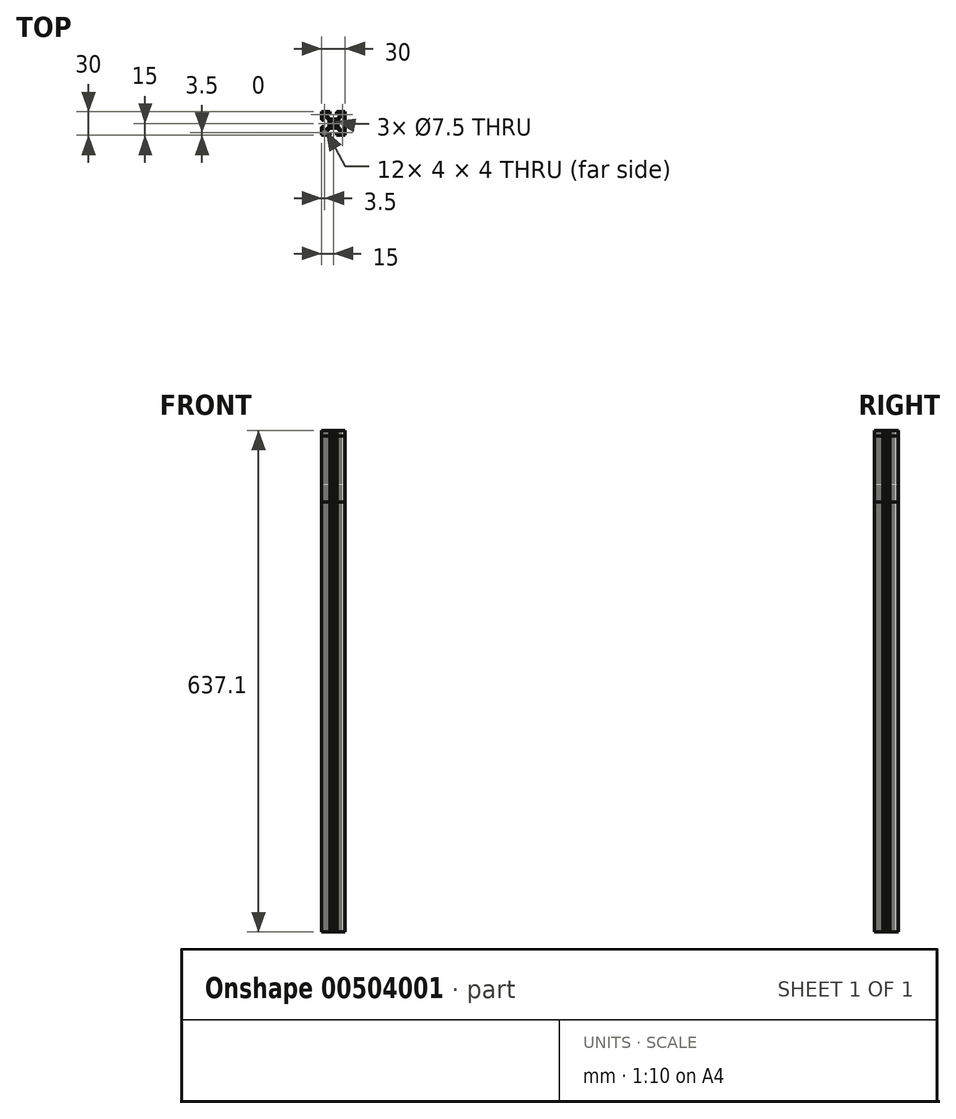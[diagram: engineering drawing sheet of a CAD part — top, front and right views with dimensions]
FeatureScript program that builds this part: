
annotation { "Feature Type Name" : "Feature", "Feature Type Description" : "" }
export const myFeature = defineFeature(function(context is Context, id is Id, definition is map)
    precondition{}
    {
        {
            assignVariable(context, id + "F0", {"name" : "Y", "anyValue" : 630});
        }
        {
            var Q0;
            Q0=qCreatedBy(makeId("Top.planeOp"),FACE);
            var sketch = newSketch(context, id + "F1", { "sketchPlane" : qUnion([Q0])});
            skLineSegment(sketch, "E0", {"start": v(-14.5, 4.6) * mm, "end": v(-15, 4.6) * mm});
            skLineSegment(sketch, "E1", {"start": v(-14.5, 4.1) * mm, "end": v(-14.5, 4.6) * mm});
            skLineSegment(sketch, "E2", {"start": v(-12.8, 4.1) * mm, "end": v(-14.5, 4.1) * mm});
            skLineSegment(sketch, "E3", {"start": v(-12.8, 8.4) * mm, "end": v(-12.8, 4.1) * mm});
            skLineSegment(sketch, "E4", {"start": v(-9.81, 8.4) * mm, "end": v(-12.8, 8.4) * mm});
            skLineSegment(sketch, "E5", {"start": v(-5.75, 0.5) * mm, "end": v(-5.75, 4.34) * mm});
            skLineSegment(sketch, "E6", {"start": v(-5.25, 0) * mm, "end": v(-5.75, 0.5) * mm});
            skLineSegment(sketch, "E7", {"start": v(-5.75, -0.5) * mm, "end": v(-5.25, 0) * mm});
            skLineSegment(sketch, "E8", {"start": v(-5.75, -4.34) * mm, "end": v(-5.75, -0.5) * mm});
            skLineSegment(sketch, "E9", {"start": v(-12.8, -8.4) * mm, "end": v(-9.81, -8.4) * mm});
            skLineSegment(sketch, "E10", {"start": v(-12.8, -4.1) * mm, "end": v(-12.8, -8.4) * mm});
            skLineSegment(sketch, "E11", {"start": v(-14.5, -4.1) * mm, "end": v(-12.8, -4.1) * mm});
            skLineSegment(sketch, "E12", {"start": v(-14.5, -4.6) * mm, "end": v(-14.5, -4.1) * mm});
            skLineSegment(sketch, "E13", {"start": v(-15, -4.6) * mm, "end": v(-14.5, -4.6) * mm});
            skLineSegment(sketch, "E14", {"start": v(-4.6, -14.5) * mm, "end": v(-4.6, -15) * mm});
            skLineSegment(sketch, "E15", {"start": v(-4.1, -14.5) * mm, "end": v(-4.6, -14.5) * mm});
            skLineSegment(sketch, "E16", {"start": v(-4.1, -12.8) * mm, "end": v(-4.1, -14.5) * mm});
            skLineSegment(sketch, "E17", {"start": v(-8.4, -12.8) * mm, "end": v(-4.1, -12.8) * mm});
            skLineSegment(sketch, "E18", {"start": v(-8.4, -9.81) * mm, "end": v(-8.4, -12.8) * mm});
            skLineSegment(sketch, "E19", {"start": v(-0.5, -5.75) * mm, "end": v(-4.34, -5.75) * mm});
            skLineSegment(sketch, "E20", {"start": v(0, -5.25) * mm, "end": v(-0.5, -5.75) * mm});
            skLineSegment(sketch, "E21", {"start": v(0.5, -5.75) * mm, "end": v(0, -5.25) * mm});
            skLineSegment(sketch, "E22", {"start": v(4.34, -5.75) * mm, "end": v(0.5, -5.75) * mm});
            skLineSegment(sketch, "E23", {"start": v(8.4, -12.8) * mm, "end": v(8.4, -9.81) * mm});
            skLineSegment(sketch, "E24", {"start": v(4.1, -12.8) * mm, "end": v(8.4, -12.8) * mm});
            skLineSegment(sketch, "E25", {"start": v(4.1, -14.5) * mm, "end": v(4.1, -12.8) * mm});
            skLineSegment(sketch, "E26", {"start": v(4.6, -14.5) * mm, "end": v(4.1, -14.5) * mm});
            skLineSegment(sketch, "E27", {"start": v(4.6, -15) * mm, "end": v(4.6, -14.5) * mm});
            skLineSegment(sketch, "E28", {"start": v(14.5, -4.6) * mm, "end": v(15, -4.6) * mm});
            skLineSegment(sketch, "E29", {"start": v(14.5, -4.1) * mm, "end": v(14.5, -4.6) * mm});
            skLineSegment(sketch, "E30", {"start": v(12.8, -4.1) * mm, "end": v(14.5, -4.1) * mm});
            skLineSegment(sketch, "E31", {"start": v(12.8, -8.4) * mm, "end": v(12.8, -4.1) * mm});
            skLineSegment(sketch, "E32", {"start": v(9.81, -8.4) * mm, "end": v(12.8, -8.4) * mm});
            skLineSegment(sketch, "E33", {"start": v(5.75, -0.5) * mm, "end": v(5.75, -4.34) * mm});
            skLineSegment(sketch, "E34", {"start": v(5.25, 0) * mm, "end": v(5.75, -0.5) * mm});
            skLineSegment(sketch, "E35", {"start": v(5.75, 0.5) * mm, "end": v(5.25, 0) * mm});
            skLineSegment(sketch, "E36", {"start": v(5.75, 4.34) * mm, "end": v(5.75, 0.5) * mm});
            skLineSegment(sketch, "E37", {"start": v(12.8, 8.4) * mm, "end": v(9.81, 8.4) * mm});
            skLineSegment(sketch, "E38", {"start": v(12.8, 4.1) * mm, "end": v(12.8, 8.4) * mm});
            skLineSegment(sketch, "E39", {"start": v(14.5, 4.1) * mm, "end": v(12.8, 4.1) * mm});
            skLineSegment(sketch, "E40", {"start": v(14.5, 4.6) * mm, "end": v(14.5, 4.1) * mm});
            skLineSegment(sketch, "E41", {"start": v(15, 4.6) * mm, "end": v(14.5, 4.6) * mm});
            skLineSegment(sketch, "E42", {"start": v(4.6, 14.5) * mm, "end": v(4.6, 15) * mm});
            skLineSegment(sketch, "E43", {"start": v(4.1, 14.5) * mm, "end": v(4.6, 14.5) * mm});
            skLineSegment(sketch, "E44", {"start": v(4.1, 12.8) * mm, "end": v(4.1, 14.5) * mm});
            skLineSegment(sketch, "E45", {"start": v(8.4, 12.8) * mm, "end": v(4.1, 12.8) * mm});
            skLineSegment(sketch, "E46", {"start": v(8.4, 9.81) * mm, "end": v(8.4, 12.8) * mm});
            skLineSegment(sketch, "E47", {"start": v(0.5, 5.75) * mm, "end": v(4.34, 5.75) * mm});
            skLineSegment(sketch, "E48", {"start": v(0, 5.25) * mm, "end": v(0.5, 5.75) * mm});
            skLineSegment(sketch, "E49", {"start": v(-0.5, 5.75) * mm, "end": v(0, 5.25) * mm});
            skLineSegment(sketch, "E50", {"start": v(-4.34, 5.75) * mm, "end": v(-0.5, 5.75) * mm});
            skLineSegment(sketch, "E51", {"start": v(-8.4, 12.8) * mm, "end": v(-8.4, 9.81) * mm});
            skLineSegment(sketch, "E52", {"start": v(-4.1, 12.8) * mm, "end": v(-8.4, 12.8) * mm});
            skLineSegment(sketch, "E53", {"start": v(-4.1, 14.5) * mm, "end": v(-4.1, 12.8) * mm});
            skLineSegment(sketch, "E54", {"start": v(-4.6, 14.5) * mm, "end": v(-4.1, 14.5) * mm});
            skLineSegment(sketch, "E55", {"start": v(-4.6, 15) * mm, "end": v(-4.6, 14.5) * mm});
            skLineSegment(sketch, "E56", {"start": v(13.5, 13.5) * mm, "end": v(9.5, 13.5) * mm});
            skLineSegment(sketch, "E57", {"start": v(13.5, 9.5) * mm, "end": v(13.5, 13.5) * mm});
            skLineSegment(sketch, "E58", {"start": v(9.5, 9.5) * mm, "end": v(13.5, 9.5) * mm});
            skLineSegment(sketch, "E59", {"start": v(9.5, 13.5) * mm, "end": v(9.5, 9.5) * mm});
            skLineSegment(sketch, "E60", {"start": v(-9.5, 9.5) * mm, "end": v(-9.5, 13.5) * mm});
            skLineSegment(sketch, "E61", {"start": v(-13.5, 9.5) * mm, "end": v(-9.5, 9.5) * mm});
            skLineSegment(sketch, "E62", {"start": v(-13.5, 13.5) * mm, "end": v(-13.5, 9.5) * mm});
            skLineSegment(sketch, "E63", {"start": v(-9.5, 13.5) * mm, "end": v(-13.5, 13.5) * mm});
            skLineSegment(sketch, "E64", {"start": v(-9.5, -13.5) * mm, "end": v(-9.5, -9.5) * mm});
            skLineSegment(sketch, "E65", {"start": v(-13.5, -13.5) * mm, "end": v(-9.5, -13.5) * mm});
            skLineSegment(sketch, "E66", {"start": v(-13.5, -9.5) * mm, "end": v(-13.5, -13.5) * mm});
            skLineSegment(sketch, "E67", {"start": v(-9.5, -9.5) * mm, "end": v(-13.5, -9.5) * mm});
            skLineSegment(sketch, "E68", {"start": v(13.5, -9.5) * mm, "end": v(9.5, -9.5) * mm});
            skLineSegment(sketch, "E69", {"start": v(13.5, -13.5) * mm, "end": v(13.5, -9.5) * mm});
            skLineSegment(sketch, "E70", {"start": v(9.5, -13.5) * mm, "end": v(13.5, -13.5) * mm});
            skLineSegment(sketch, "E71", {"start": v(9.5, -9.5) * mm, "end": v(9.5, -13.5) * mm});
            skCircle(sketch, "E72", {"center": v(0, 0) * mm, "radius": 3.75 * mm});
            skLineSegment(sketch, "E73", {"start": v(-15, -4.6) * mm, "end": v(-15, -15) * mm});
            skLineSegment(sketch, "E74", {"start": v(15, -4.6) * mm, "end": v(15, -15) * mm});
            skLineSegment(sketch, "E75", {"start": v(-4.6, -15) * mm, "end": v(-15, -15) * mm});
            skLineSegment(sketch, "E76", {"start": v(-9.81, -8.4) * mm, "end": v(-5.75, -4.34) * mm});
            skLineSegment(sketch, "E77", {"start": v(-8.4, -9.81) * mm, "end": v(-4.34, -5.75) * mm});
            skLineSegment(sketch, "E78", {"start": v(4.6, -15) * mm, "end": v(15, -15) * mm});
            skLineSegment(sketch, "E79", {"start": v(4.34, -5.75) * mm, "end": v(8.4, -9.81) * mm});
            skLineSegment(sketch, "E80", {"start": v(5.75, -4.34) * mm, "end": v(9.81, -8.4) * mm});
            skLineSegment(sketch, "E81", {"start": v(9.81, 8.4) * mm, "end": v(5.75, 4.34) * mm});
            skLineSegment(sketch, "E82", {"start": v(8.4, 9.81) * mm, "end": v(4.34, 5.75) * mm});
            skLineSegment(sketch, "E83", {"start": v(-9.81, 8.4) * mm, "end": v(-5.75, 4.34) * mm});
            skLineSegment(sketch, "E84", {"start": v(-8.4, 9.81) * mm, "end": v(-4.34, 5.75) * mm});
            skLineSegment(sketch, "E85", {"start": v(-15, 4.6) * mm, "end": v(-15, 15) * mm});
            skLineSegment(sketch, "E86", {"start": v(15, 4.6) * mm, "end": v(15, 15) * mm});
            skLineSegment(sketch, "E87", {"start": v(-4.6, 15) * mm, "end": v(-15, 15) * mm});
            skLineSegment(sketch, "E88", {"start": v(15, 15) * mm, "end": v(4.6, 15) * mm});
            skSolve(sketch);
        }
        {
            var Q0;
            Q0=makeQuery(id+"F1.imprint","IMPRINT",FACE,{"disambiguationData":[TD([[makeQuery(id+"F1.imprint","IMPRINT",EDGE,{"derivedFrom":sQuery(id+"F1.wireOp",EDGE,"E0")}),-1.0]])]});
            extrude(context, id + "F2", {"entities" : qUnion([Q0]), "depth" : 546 * mm, "offsetDistance" : 25 * mm});
        }
        {
            var Q0;
            Q0=qCreatedBy(makeId("Top.planeOp"),FACE);
            var sketch = newSketch(context, id + "F3", { "sketchPlane" : qUnion([Q0])});
            skLineSegment(sketch, "E89", {"start": v(-14.5, 4.6) * mm, "end": v(-15, 4.6) * mm});
            skLineSegment(sketch, "E90", {"start": v(-14.5, 4.1) * mm, "end": v(-14.5, 4.6) * mm});
            skLineSegment(sketch, "E91", {"start": v(-12.8, 4.1) * mm, "end": v(-14.5, 4.1) * mm});
            skLineSegment(sketch, "E92", {"start": v(-12.8, 8.4) * mm, "end": v(-12.8, 4.1) * mm});
            skLineSegment(sketch, "E93", {"start": v(-9.81, 8.4) * mm, "end": v(-12.8, 8.4) * mm});
            skLineSegment(sketch, "E94", {"start": v(-5.75, 0.5) * mm, "end": v(-5.75, 4.34) * mm});
            skLineSegment(sketch, "E95", {"start": v(-5.25, 0) * mm, "end": v(-5.75, 0.5) * mm});
            skLineSegment(sketch, "E96", {"start": v(-5.75, -0.5) * mm, "end": v(-5.25, 0) * mm});
            skLineSegment(sketch, "E97", {"start": v(-5.75, -4.34) * mm, "end": v(-5.75, -0.5) * mm});
            skLineSegment(sketch, "E98", {"start": v(-12.8, -8.4) * mm, "end": v(-9.81, -8.4) * mm});
            skLineSegment(sketch, "E99", {"start": v(-12.8, -4.1) * mm, "end": v(-12.8, -8.4) * mm});
            skLineSegment(sketch, "E100", {"start": v(-14.5, -4.1) * mm, "end": v(-12.8, -4.1) * mm});
            skLineSegment(sketch, "E101", {"start": v(-14.5, -4.6) * mm, "end": v(-14.5, -4.1) * mm});
            skLineSegment(sketch, "E102", {"start": v(-15, -4.6) * mm, "end": v(-14.5, -4.6) * mm});
            skLineSegment(sketch, "E103", {"start": v(-4.6, -14.5) * mm, "end": v(-4.6, -15) * mm});
            skLineSegment(sketch, "E104", {"start": v(-4.1, -14.5) * mm, "end": v(-4.6, -14.5) * mm});
            skLineSegment(sketch, "E105", {"start": v(-4.1, -12.8) * mm, "end": v(-4.1, -14.5) * mm});
            skLineSegment(sketch, "E106", {"start": v(-8.4, -12.8) * mm, "end": v(-4.1, -12.8) * mm});
            skLineSegment(sketch, "E107", {"start": v(-8.4, -9.81) * mm, "end": v(-8.4, -12.8) * mm});
            skLineSegment(sketch, "E108", {"start": v(-0.5, -5.75) * mm, "end": v(-4.34, -5.75) * mm});
            skLineSegment(sketch, "E109", {"start": v(0, -5.25) * mm, "end": v(-0.5, -5.75) * mm});
            skLineSegment(sketch, "E110", {"start": v(0.5, -5.75) * mm, "end": v(0, -5.25) * mm});
            skLineSegment(sketch, "E111", {"start": v(4.34, -5.75) * mm, "end": v(0.5, -5.75) * mm});
            skLineSegment(sketch, "E112", {"start": v(8.4, -12.8) * mm, "end": v(8.4, -9.81) * mm});
            skLineSegment(sketch, "E113", {"start": v(4.1, -12.8) * mm, "end": v(8.4, -12.8) * mm});
            skLineSegment(sketch, "E114", {"start": v(4.1, -14.5) * mm, "end": v(4.1, -12.8) * mm});
            skLineSegment(sketch, "E115", {"start": v(4.6, -14.5) * mm, "end": v(4.1, -14.5) * mm});
            skLineSegment(sketch, "E116", {"start": v(4.6, -15) * mm, "end": v(4.6, -14.5) * mm});
            skLineSegment(sketch, "E117", {"start": v(14.5, -4.6) * mm, "end": v(15, -4.6) * mm});
            skLineSegment(sketch, "E118", {"start": v(14.5, -4.1) * mm, "end": v(14.5, -4.6) * mm});
            skLineSegment(sketch, "E119", {"start": v(12.8, -4.1) * mm, "end": v(14.5, -4.1) * mm});
            skLineSegment(sketch, "E120", {"start": v(12.8, -8.4) * mm, "end": v(12.8, -4.1) * mm});
            skLineSegment(sketch, "E121", {"start": v(9.81, -8.4) * mm, "end": v(12.8, -8.4) * mm});
            skLineSegment(sketch, "E122", {"start": v(5.75, -0.5) * mm, "end": v(5.75, -4.34) * mm});
            skLineSegment(sketch, "E123", {"start": v(5.25, 0) * mm, "end": v(5.75, -0.5) * mm});
            skLineSegment(sketch, "E124", {"start": v(5.75, 0.5) * mm, "end": v(5.25, 0) * mm});
            skLineSegment(sketch, "E125", {"start": v(5.75, 4.34) * mm, "end": v(5.75, 0.5) * mm});
            skLineSegment(sketch, "E126", {"start": v(12.8, 8.4) * mm, "end": v(9.81, 8.4) * mm});
            skLineSegment(sketch, "E127", {"start": v(12.8, 4.1) * mm, "end": v(12.8, 8.4) * mm});
            skLineSegment(sketch, "E128", {"start": v(14.5, 4.1) * mm, "end": v(12.8, 4.1) * mm});
            skLineSegment(sketch, "E129", {"start": v(14.5, 4.6) * mm, "end": v(14.5, 4.1) * mm});
            skLineSegment(sketch, "E130", {"start": v(15, 4.6) * mm, "end": v(14.5, 4.6) * mm});
            skLineSegment(sketch, "E131", {"start": v(4.6, 14.5) * mm, "end": v(4.6, 15) * mm});
            skLineSegment(sketch, "E132", {"start": v(4.1, 14.5) * mm, "end": v(4.6, 14.5) * mm});
            skLineSegment(sketch, "E133", {"start": v(4.1, 12.8) * mm, "end": v(4.1, 14.5) * mm});
            skLineSegment(sketch, "E134", {"start": v(8.4, 12.8) * mm, "end": v(4.1, 12.8) * mm});
            skLineSegment(sketch, "E135", {"start": v(8.4, 9.81) * mm, "end": v(8.4, 12.8) * mm});
            skLineSegment(sketch, "E136", {"start": v(0.5, 5.75) * mm, "end": v(4.34, 5.75) * mm});
            skLineSegment(sketch, "E137", {"start": v(0, 5.25) * mm, "end": v(0.5, 5.75) * mm});
            skLineSegment(sketch, "E138", {"start": v(-0.5, 5.75) * mm, "end": v(0, 5.25) * mm});
            skLineSegment(sketch, "E139", {"start": v(-4.34, 5.75) * mm, "end": v(-0.5, 5.75) * mm});
            skLineSegment(sketch, "E140", {"start": v(-8.4, 12.8) * mm, "end": v(-8.4, 9.81) * mm});
            skLineSegment(sketch, "E141", {"start": v(-4.1, 12.8) * mm, "end": v(-8.4, 12.8) * mm});
            skLineSegment(sketch, "E142", {"start": v(-4.1, 14.5) * mm, "end": v(-4.1, 12.8) * mm});
            skLineSegment(sketch, "E143", {"start": v(-4.6, 14.5) * mm, "end": v(-4.1, 14.5) * mm});
            skLineSegment(sketch, "E144", {"start": v(-4.6, 15) * mm, "end": v(-4.6, 14.5) * mm});
            skLineSegment(sketch, "E145", {"start": v(13.5, 13.5) * mm, "end": v(9.5, 13.5) * mm});
            skLineSegment(sketch, "E146", {"start": v(13.5, 9.5) * mm, "end": v(13.5, 13.5) * mm});
            skLineSegment(sketch, "E147", {"start": v(9.5, 9.5) * mm, "end": v(13.5, 9.5) * mm});
            skLineSegment(sketch, "E148", {"start": v(9.5, 13.5) * mm, "end": v(9.5, 9.5) * mm});
            skLineSegment(sketch, "E149", {"start": v(-9.5, 9.5) * mm, "end": v(-9.5, 13.5) * mm});
            skLineSegment(sketch, "E150", {"start": v(-13.5, 9.5) * mm, "end": v(-9.5, 9.5) * mm});
            skLineSegment(sketch, "E151", {"start": v(-13.5, 13.5) * mm, "end": v(-13.5, 9.5) * mm});
            skLineSegment(sketch, "E152", {"start": v(-9.5, 13.5) * mm, "end": v(-13.5, 13.5) * mm});
            skLineSegment(sketch, "E153", {"start": v(-9.5, -13.5) * mm, "end": v(-9.5, -9.5) * mm});
            skLineSegment(sketch, "E154", {"start": v(-13.5, -13.5) * mm, "end": v(-9.5, -13.5) * mm});
            skLineSegment(sketch, "E155", {"start": v(-13.5, -9.5) * mm, "end": v(-13.5, -13.5) * mm});
            skLineSegment(sketch, "E156", {"start": v(-9.5, -9.5) * mm, "end": v(-13.5, -9.5) * mm});
            skLineSegment(sketch, "E157", {"start": v(13.5, -9.5) * mm, "end": v(9.5, -9.5) * mm});
            skLineSegment(sketch, "E158", {"start": v(13.5, -13.5) * mm, "end": v(13.5, -9.5) * mm});
            skLineSegment(sketch, "E159", {"start": v(9.5, -13.5) * mm, "end": v(13.5, -13.5) * mm});
            skLineSegment(sketch, "E160", {"start": v(9.5, -9.5) * mm, "end": v(9.5, -13.5) * mm});
            skCircle(sketch, "E161", {"center": v(0, 0) * mm, "radius": 3.75 * mm});
            skLineSegment(sketch, "E162", {"start": v(-15, -4.6) * mm, "end": v(-15, -15) * mm});
            skLineSegment(sketch, "E163", {"start": v(15, -4.6) * mm, "end": v(15, -15) * mm});
            skLineSegment(sketch, "E164", {"start": v(-4.6, -15) * mm, "end": v(-15, -15) * mm});
            skLineSegment(sketch, "E165", {"start": v(-9.81, -8.4) * mm, "end": v(-5.75, -4.34) * mm});
            skLineSegment(sketch, "E166", {"start": v(-8.4, -9.81) * mm, "end": v(-4.34, -5.75) * mm});
            skLineSegment(sketch, "E167", {"start": v(4.6, -15) * mm, "end": v(15, -15) * mm});
            skLineSegment(sketch, "E168", {"start": v(4.34, -5.75) * mm, "end": v(8.4, -9.81) * mm});
            skLineSegment(sketch, "E169", {"start": v(5.75, -4.34) * mm, "end": v(9.81, -8.4) * mm});
            skLineSegment(sketch, "E170", {"start": v(9.81, 8.4) * mm, "end": v(5.75, 4.34) * mm});
            skLineSegment(sketch, "E171", {"start": v(8.4, 9.81) * mm, "end": v(4.34, 5.75) * mm});
            skLineSegment(sketch, "E172", {"start": v(-9.81, 8.4) * mm, "end": v(-5.75, 4.34) * mm});
            skLineSegment(sketch, "E173", {"start": v(-8.4, 9.81) * mm, "end": v(-4.34, 5.75) * mm});
            skLineSegment(sketch, "E174", {"start": v(-15, 4.6) * mm, "end": v(-15, 15) * mm});
            skLineSegment(sketch, "E175", {"start": v(15, 4.6) * mm, "end": v(15, 15) * mm});
            skLineSegment(sketch, "E176", {"start": v(-4.6, 15) * mm, "end": v(-15, 15) * mm});
            skLineSegment(sketch, "E177", {"start": v(15, 15) * mm, "end": v(4.6, 15) * mm});
            skSolve(sketch);
        }
        {
            var Q0;
            Q0 = qSketchRegion(id + "F3", true);
            extrude(context, id + "F4", {"entities" : qUnion([Q0]), "flatOperationType" : FlatOperationType.REMOVE, "depth" : (getVariable(context, 'Y')) * mm, "offsetDistance" : 25 * mm, "domain" : OperationDomain.MODEL});
        }
        {
            var Q0;
            Q0 = qSketchRegion(id + "F3", true);
            extrude(context, id + "F5", {"entities" : qUnion([Q0]), "depth" : 637.1 * mm, "offsetDistance" : 25 * mm});
        }
    });
